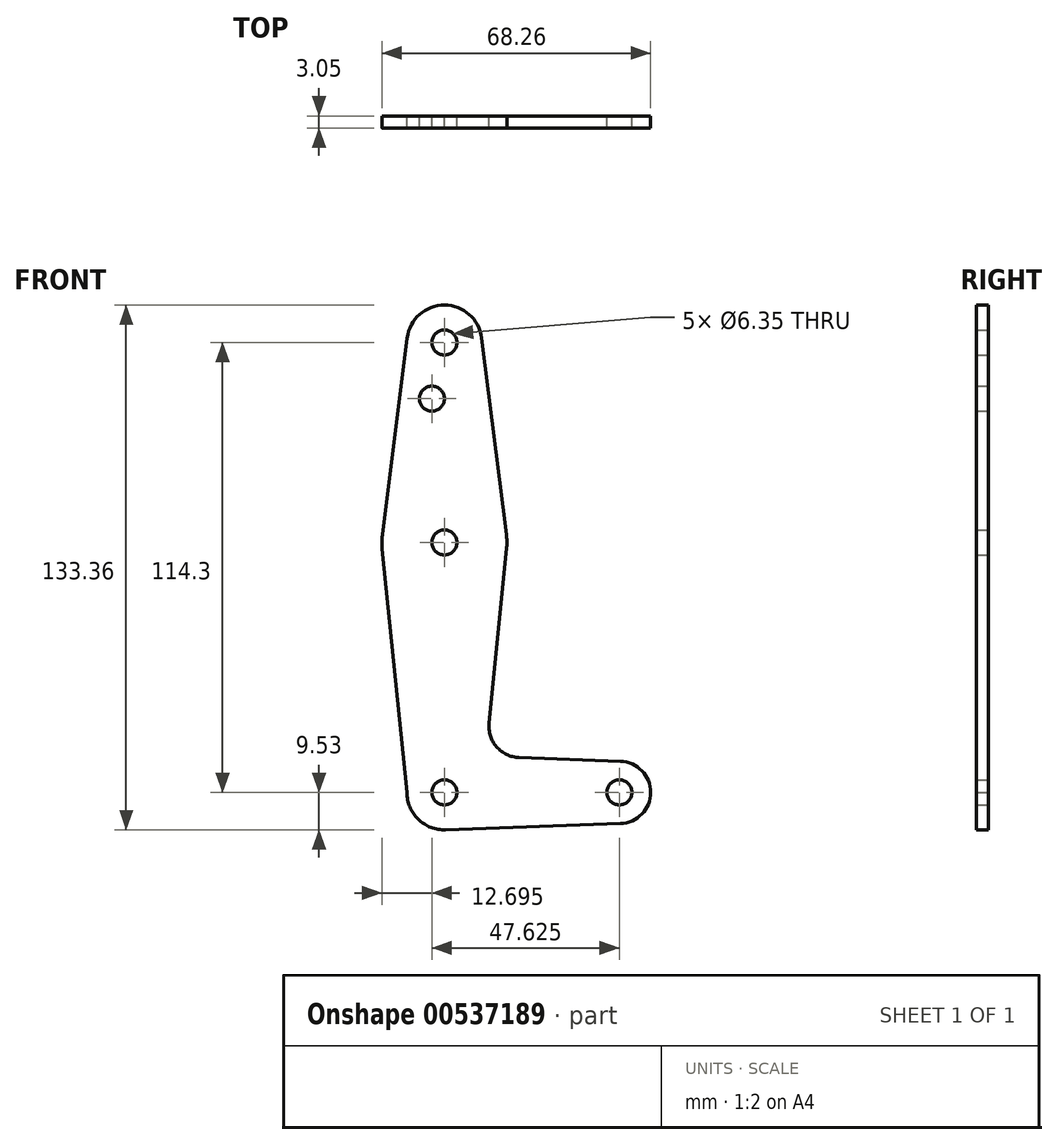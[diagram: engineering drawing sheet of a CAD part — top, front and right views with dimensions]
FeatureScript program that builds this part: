
annotation { "Feature Type Name" : "Feature", "Feature Type Description" : "" }
export const myFeature = defineFeature(function(context is Context, id is Id, definition is map)
    precondition{}
    {
        {
            var Q0;
            Q0=qCreatedBy(makeId("Front.planeOp"),FACE);
            var sketch = newSketch(context, id + "F0", { "sketchPlane" : qUnion([Q0])});
            skLineSegment(sketch, "E0", {"start": v(0, 0) * mm, "end": v(0, 114.3) * mm, "construction": true});
            skLineSegment(sketch, "E1", {"start": v(0, 0) * mm, "end": v(44.45, 0) * mm, "construction": true});
            skCircle(sketch, "E2", {"center": v(0, 114.3) * mm, "radius": 9.52 * mm});
            skCircle(sketch, "E3", {"center": v(0, 0) * mm, "radius": 9.52 * mm});
            skCircle(sketch, "E4", {"center": v(44.45, 0) * mm, "radius": 7.94 * mm});
            skCircle(sketch, "E5", {"center": v(0, 63.5) * mm, "radius": 15.88 * mm});
            skLineSegment(sketch, "E6", {"start": v(-9.45, 115.5) * mm, "end": v(-15.75, 65.48) * mm});
            skLineSegment(sketch, "E7", {"start": v(-15.8, 61.9) * mm, "end": v(-9.52, 0) * mm});
            skLineSegment(sketch, "E8", {"start": v(9.45, 115.5) * mm, "end": v(15.75, 65.48) * mm});
            skLineSegment(sketch, "E9", {"start": v(11.34, 17.6) * mm, "end": v(15.8, 61.91) * mm});
            skLineSegment(sketch, "E10", {"start": v(18.97, 8.85) * mm, "end": v(44.73, 7.93) * mm});
            skLineSegment(sketch, "E11", {"start": v(0.34, -9.52) * mm, "end": v(44.73, -7.93) * mm});
            skCircle(sketch, "E12", {"center": v(0, 114.3) * mm, "radius": 3.18 * mm});
            skCircle(sketch, "E13", {"center": v(0, 63.5) * mm, "radius": 3.18 * mm});
            skCircle(sketch, "E14", {"center": v(0, 0) * mm, "radius": 3.18 * mm});
            skCircle(sketch, "E15", {"center": v(44.45, 0) * mm, "radius": 3.18 * mm});
            skCircle(sketch, "E16", {"center": v(-3.18, 100.03) * mm, "radius": 3.18 * mm});
            skArc(sketch, "E17.filletArc", {"start": v(11.34, 17.6) * mm, "mid": v(13.26, 11.57) * mm, "end": v(18.97, 8.85) * mm});
            skSolve(sketch);
        }
        {
            var Q0;
            Q0=qSketchRegion(id+"F0",true);
            extrude(context, id + "F1", {"entities" : qUnion([Q0]), "depth" : 3.05 * mm});
        }
    });
